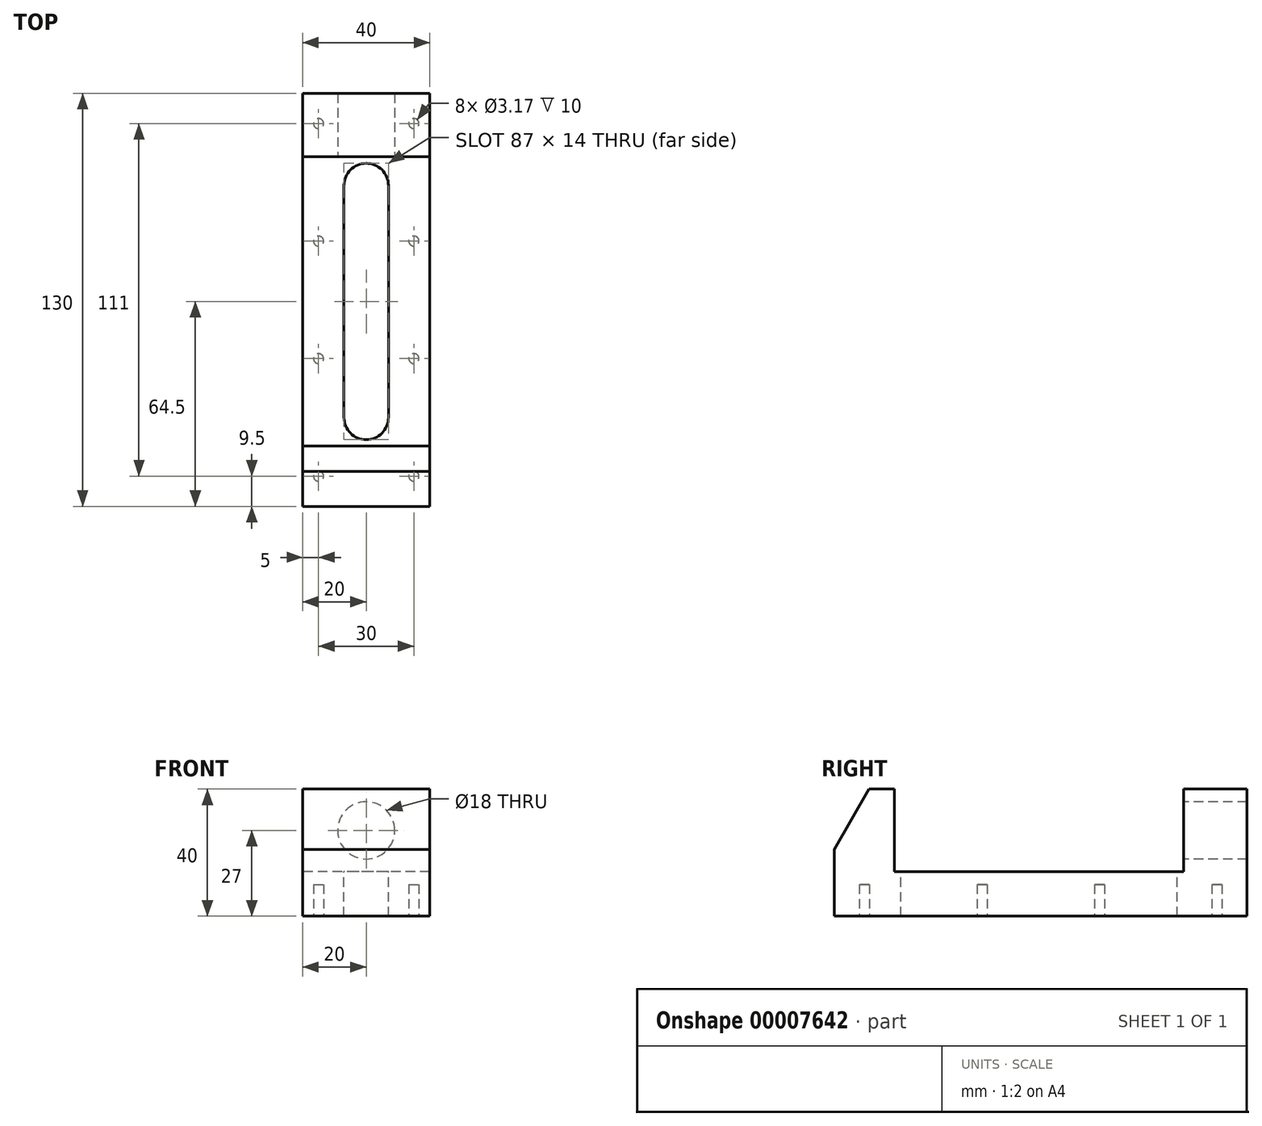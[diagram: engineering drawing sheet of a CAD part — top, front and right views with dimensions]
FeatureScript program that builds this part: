
annotation { "Feature Type Name" : "Feature", "Feature Type Description" : "" }
export const myFeature = defineFeature(function(context is Context, id is Id, definition is map)
    precondition{}
    {
        {
            var Q0;
            Q0=qCreatedBy(makeId("Right.planeOp"),FACE);
            var sketch = newSketch(context, id + "F0", { "sketchPlane" : qUnion([Q0])});
            skLineSegment(sketch, "E0", {"start": v(0, 0) * mm, "end": v(0, 40) * mm});
            skLineSegment(sketch, "E1", {"start": v(0, 40) * mm, "end": v(-20, 40) * mm});
            skLineSegment(sketch, "E2", {"start": v(-20, 40) * mm, "end": v(-20, 14) * mm});
            skLineSegment(sketch, "E3", {"start": v(-20, 14) * mm, "end": v(-111, 14) * mm});
            skLineSegment(sketch, "E4", {"start": v(-111, 14) * mm, "end": v(-111, 40) * mm});
            skLineSegment(sketch, "E5", {"start": v(-111, 40) * mm, "end": v(-119, 40) * mm});
            skLineSegment(sketch, "E6", {"start": v(-119, 40) * mm, "end": v(-130, 20.95) * mm});
            skLineSegment(sketch, "E7", {"start": v(-130, 20.95) * mm, "end": v(-130, 0) * mm});
            skLineSegment(sketch, "E8", {"start": v(-130, 0) * mm, "end": v(0, 0) * mm});
            skSolve(sketch);
        }
        {
            var Q0;
            Q0 = qSketchRegion(id + "F0", true);
            extrude(context, id + "F1", {"entities" : qUnion([Q0]), "depth" : 40 * mm, "symmetric" : true});
        }
        {
            var Q0;
            Q0=makeQuery(id+"F1.opExtrude","SWEPT_FACE",FACE,{"disambiguationData":[OSD([sQuery(id+"F0.wireOp",EDGE,"E3")])]});
            var sketch = newSketch(context, id + "F2", { "sketchPlane" : qUnion([Q0])});
            skLineSegment(sketch, "E9", {"start": v(-7, -102) * mm, "end": v(-7, -29) * mm});
            skArc(sketch, "E10", {"start": v(-7, -29) * mm, "mid": v(0, -22) * mm, "end": v(7, -29) * mm});
            skLineSegment(sketch, "E11", {"start": v(7, -29) * mm, "end": v(7, -102) * mm});
            skArc(sketch, "E12", {"start": v(7, -102) * mm, "mid": v(0, -109) * mm, "end": v(-7, -102) * mm});
            skSolve(sketch);
        }
        {
            var Q0;
            Q0 = qSketchRegion(id + "F2", true);
            extrude(context, id + "F3", {"entities" : qUnion([Q0]), "operationType" : NewBodyOperationType.REMOVE, "endBound" : BoundingType.THROUGH_ALL, "oppositeDirection" : true, "depth" : 25 * mm});
        }
        {
            var Q0;
            Q0=makeQuery(id+"F1.opExtrude","SWEPT_FACE",FACE,{"disambiguationData":[OSD([sQuery(id+"F0.wireOp",EDGE,"E2")])]});
            var sketch = newSketch(context, id + "F4", { "sketchPlane" : qUnion([Q0])});
            skCircle(sketch, "E13", {"center": v(0, 27) * mm, "radius": 9 * mm});
            skSolve(sketch);
        }
        {
            var Q0;
            Q0 = qSketchRegion(id + "F4", true);
            extrude(context, id + "F5", {"entities" : qUnion([Q0]), "operationType" : NewBodyOperationType.REMOVE, "endBound" : BoundingType.THROUGH_ALL, "oppositeDirection" : true, "depth" : 25 * mm});
        }
        {
            var Q0;
            Q0=makeQuery(id+"F1.opExtrude","SWEPT_FACE",FACE,{"disambiguationData":[OSD([sQuery(id+"F0.wireOp",EDGE,"E8")])]});
            var sketch = newSketch(context, id + "F6", { "sketchPlane" : qUnion([Q0])});
            skCircle(sketch, "E14", {"center": v(-15, 120.5) * mm, "radius": 1.59 * mm});
            skCircle(sketch, "E15.0.1.0", {"center": v(-15, 83.5) * mm, "radius": 1.59 * mm});
            skCircle(sketch, "E15.0.2.0", {"center": v(-15, 46.5) * mm, "radius": 1.59 * mm});
            skCircle(sketch, "E15.0.3.0", {"center": v(-15, 9.5) * mm, "radius": 1.59 * mm});
            skCircle(sketch, "E15.1.0.0", {"center": v(15, 120.5) * mm, "radius": 1.59 * mm});
            skCircle(sketch, "E15.1.1.0", {"center": v(15, 83.5) * mm, "radius": 1.59 * mm});
            skCircle(sketch, "E15.1.2.0", {"center": v(15, 46.5) * mm, "radius": 1.59 * mm});
            skCircle(sketch, "E15.1.3.0", {"center": v(15, 9.5) * mm, "radius": 1.59 * mm});
            skLineSegment(sketch, "E15.direction1", {"start": v(-15, 120.5) * mm, "end": v(15, 120.5) * mm, "construction": true});
            skLineSegment(sketch, "E15.direction2", {"start": v(-15, 120.5) * mm, "end": v(-15, 83.5) * mm, "construction": true});
            skSolve(sketch);
        }
        {
            var Q0;
            Q0 = qSketchRegion(id + "F6", true);
            extrude(context, id + "F7", {"entities" : qUnion([Q0]), "operationType" : NewBodyOperationType.REMOVE, "oppositeDirection" : true, "depth" : 10 * mm});
        }
    });
